# Revit family: zzzBottle_Filler-Pedestal_Mounted-Murdock_Mfg-MOBF_Series.rfa
name_source: partatom
category: Plumbing Fixtures
units: mm (PartAtom-declared; Revit-internal decimal feet)

## family parameters
Cut with Voids When Loaded = No
Host = Face
OmniClass Number = 23.65.70.14.11
OmniClass Title = Drinking Fountains/Coolers
Part Type = Normal
Room Calculation Point = No
Round Connector Dimension = Use Diameter
Shared = Yes

## types (8) — shared parameters
-FRU1  Underground freeze-resistant single valve = No
-FRU2  Underground freeze-resistant double valves = No
-HB1 Hose bibb, compression, with hose threaded outlet/VB = No
-HB3 Hose bibb, loose key, vandal resistant, locked door with hose threaded outlet/VB = No
-IAP Inground anchor plate = No
-LOGO Customer specified logo = No
-PF Pet fountain receptor = No
ADA Compliant = Yes
Assembly Code = D2010810
CW Connection = Yes
CWFU = 1.5
Cold Water Connection Diameter = 1/2"
Compliance Certifications = ANSI A117.1,  Public Law 111-380 , (NO-LEAD)CHSC 116875 and NSF/ANSI 61, Section 9
Default Elevation = 0"
Description = Sensor Activated Stainless Steel Outdoor Pedestal Bottle Filler
Finish- Fountain Bowl = Stainless Steel-Murdock-18_Gauge-Type304-Grey
Finish-Others = Stainless Steel-Murdock-Polished
HW Connection = No
Installation Instruction Link = https://www.murdockmfg.com
Installation Type = Pedestal Mounted
Laminar (LAM) = Yes
Manufacturer = Murdock Manufacturing
Operating Pressure = 30 to 100 psi
Overall Height = 52 1/4"
Overall Width = 12"
Product Documentation Link = https://www.murdockmfg.com
Product Page URL = https://www.murdockmfg.com
Revised Date = 02/14/2022
URL = http://www.murdockmfg.com
Vent Connection = No
WFU = 2
Warranty Documentation Link = https://www.murdockmfg.com
Waste Connection = Yes
Waste Connection Diameter = 1 1/2"
Water Pressure = 20-105 psig
cUPC Compliant = Yes
zero-valued in all types: HWFU

## per-type parameters (varying)
| type | Activation | Finish | Material | Sensor |
| M-OBF5 | Sensor or Push Button | Stainless_Steel-Murdock-12_Gauge-Green_Powder_Coated | Stainless_Steel-Murdock-12_Gauge-Green_Powder_Coated | Yes |
| M-OBFM5 | Push-button Operated | Stainless_Steel-Murdock-12_Gauge-Green_Powder_Coated | Stainless_Steel-Murdock-12_Gauge-Green_Powder_Coated | No |
| M-OBF6 | Sensor or Push Button | Stainless_Steel-Murdock-12_Gauge-Red_Powder_Coated | Stainless_Steel-Murdock-12_Gauge-Red_Powder_Coated | Yes |
| M-OBFM6 | Push-button Operated | Stainless_Steel-Murdock-12_Gauge-Red_Powder_Coated | Stainless_Steel-Murdock-12_Gauge-Red_Powder_Coated | No |
| M-OBF7 | Sensor or Push Button | Stainless_Steel-Murdock-12_Gauge-Blue_Powder_Coated | Stainless_Steel-Murdock-12_Gauge-Blue_Powder_Coated | Yes |
| M-OBFM7 | Push-button Operated | Stainless_Steel-Murdock-12_Gauge-Blue_Powder_Coated | Stainless_Steel-Murdock-12_Gauge-Blue_Powder_Coated | No |
| M-OBF4 | Sensor or Push Button | Stainless Steel-Murdock-Satin | Stainless Steel-Murdock-Satin | Yes |
| M-OBFM4 | Push-button Operated | Stainless Steel-Murdock-Satin | Stainless Steel-Murdock-Satin | No |

note: column(s) folded — value = type name in every type: Model

## geometry (parser evidence)
native form markers: Sweep x2
no freeform markers — native parametric forms only
